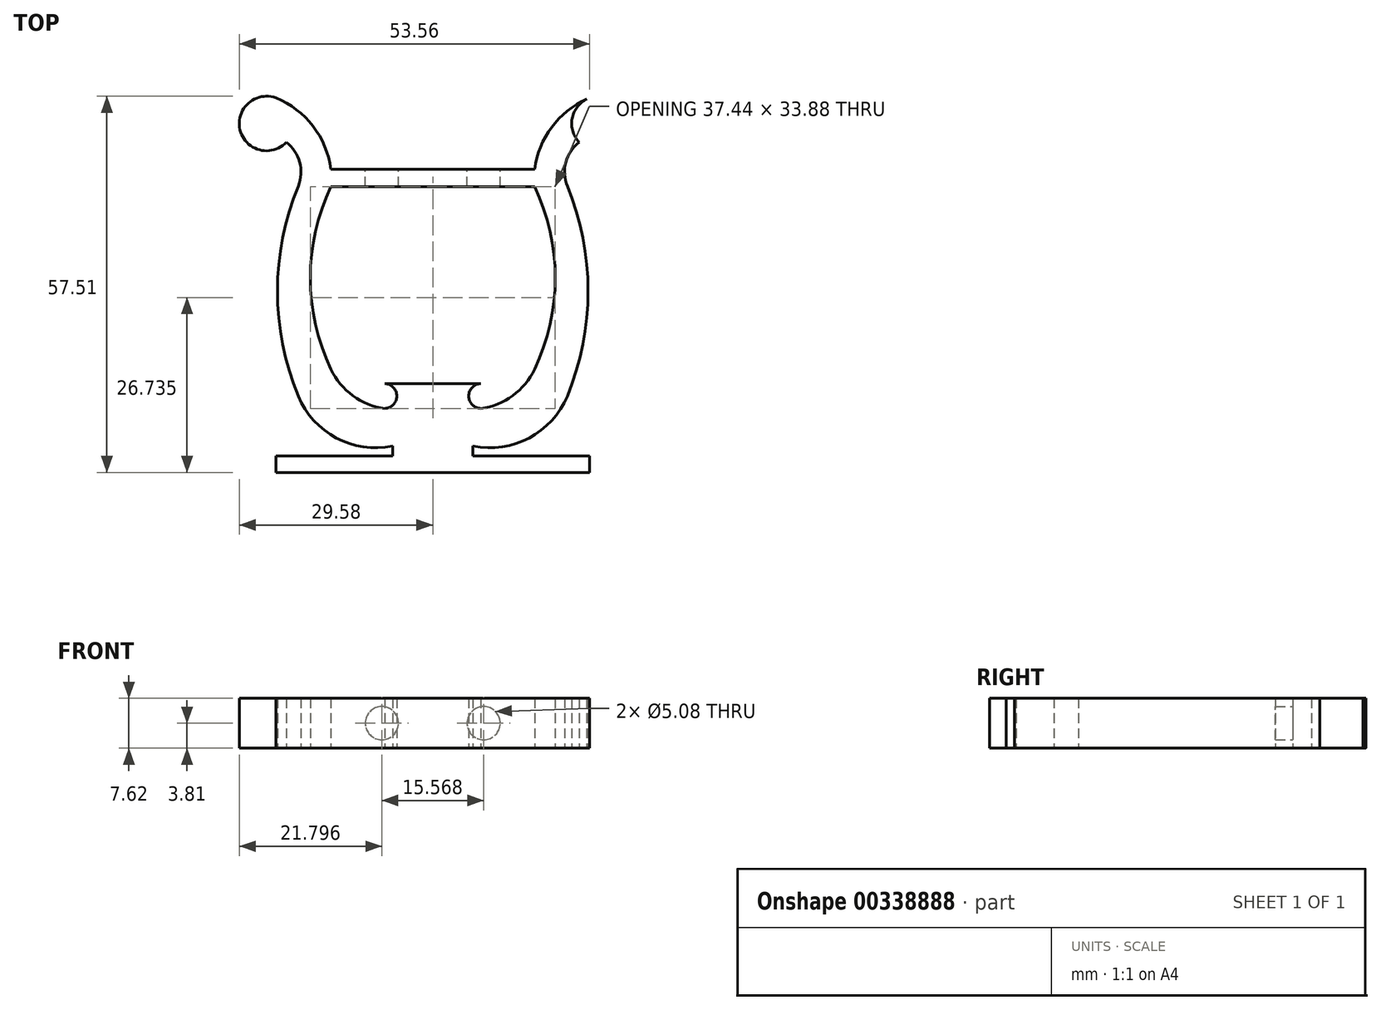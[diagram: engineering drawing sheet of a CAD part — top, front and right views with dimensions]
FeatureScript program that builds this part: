
annotation { "Feature Type Name" : "Feature", "Feature Type Description" : "" }
export const myFeature = defineFeature(function(context is Context, id is Id, definition is map)
    precondition{}
    {
        {
            var Q0;
            Q0=qCreatedBy(makeId("Top.planeOp"),FACE);
            var sketch = newSketch(context, id + "F0", { "sketchPlane" : qUnion([Q0])});
            skLineSegment(sketch, "E0", {"start": v(0, 25.38) * mm, "end": v(0, -25.42) * mm});
            skCircle(sketch, "E1", {"center": v(-25.4, 25.38) * mm, "radius": 4.17 * mm});
            skArc(sketch, "E2", {"start": v(-15.57, 18.4) * mm, "mid": v(-18.31, 24.98) * mm, "end": v(-23.98, 29.3) * mm});
            skArc(sketch, "E3", {"start": v(-20.58, 15.8) * mm, "mid": v(-20.35, 19.46) * mm, "end": v(-22.37, 22.51) * mm});
            skLineSegment(sketch, "E4", {"start": v(0, 18.4) * mm, "end": v(-15.57, 18.4) * mm});
            skLineSegment(sketch, "E5", {"start": v(0, 15.72) * mm, "end": v(-15.57, 15.72) * mm});
            skArc(sketch, "E6", {"start": v(-15.57, 15.72) * mm, "mid": v(-18.72, 1.77) * mm, "end": v(-15.57, -12.17) * mm});
            skArc(sketch, "E7", {"start": v(-20.58, 15.8) * mm, "mid": v(-23.74, -0.24) * mm, "end": v(-20.58, -16.28) * mm});
            skArc(sketch, "E8", {"start": v(-15.57, -12.17) * mm, "mid": v(-12.22, -16.21) * mm, "end": v(-7.35, -18.17) * mm});
            skArc(sketch, "E9", {"start": v(-7.35, -18.17) * mm, "mid": v(-5.5, -16.27) * mm, "end": v(-7.35, -14.37) * mm});
            skLineSegment(sketch, "E10", {"start": v(-7.35, -14.37) * mm, "end": v(0, -14.37) * mm});
            skArc(sketch, "E11", {"start": v(-20.58, -16.28) * mm, "mid": v(-14.74, -22.69) * mm, "end": v(-6.15, -23.9) * mm});
            skLineSegment(sketch, "E12", {"start": v(-6.15, -23.9) * mm, "end": v(-6.15, -25.42) * mm});
            skLineSegment(sketch, "E13", {"start": v(-6.15, -25.42) * mm, "end": v(-23.98, -25.42) * mm});
            skLineSegment(sketch, "E14", {"start": v(-23.98, -25.42) * mm, "end": v(-23.98, -27.96) * mm});
            skLineSegment(sketch, "E15", {"start": v(-23.98, -27.96) * mm, "end": v(0, -27.96) * mm});
            skArc(sketch, "E16.MirrorCS", {"start": v(15.57, 15.72) * mm, "mid": v(18.72, 1.77) * mm, "end": v(15.57, -12.17) * mm});
            skArc(sketch, "E17.MirrorCS", {"start": v(15.57, -12.17) * mm, "mid": v(12.22, -16.21) * mm, "end": v(7.35, -18.17) * mm});
            skLineSegment(sketch, "E18.MirrorCS", {"start": v(7.35, -14.37) * mm, "end": v(0, -14.37) * mm});
            skArc(sketch, "E19.MirrorCS", {"start": v(7.35, -18.17) * mm, "mid": v(5.5, -16.27) * mm, "end": v(7.35, -14.37) * mm});
            skArc(sketch, "E20.MirrorCS", {"start": v(20.58, -16.28) * mm, "mid": v(14.74, -22.69) * mm, "end": v(6.15, -23.9) * mm});
            skLineSegment(sketch, "E21.MirrorCS", {"start": v(6.15, -25.42) * mm, "end": v(23.98, -25.42) * mm});
            skLineSegment(sketch, "E22.MirrorCS", {"start": v(23.98, -27.96) * mm, "end": v(0, -27.96) * mm});
            skArc(sketch, "E23.MirrorCS", {"start": v(20.58, 15.8) * mm, "mid": v(23.74, -0.24) * mm, "end": v(20.58, -16.28) * mm});
            skLineSegment(sketch, "E24.MirrorCS", {"start": v(0, 15.72) * mm, "end": v(15.57, 15.72) * mm});
            skLineSegment(sketch, "E25.MirrorCS", {"start": v(0, 18.4) * mm, "end": v(15.57, 18.4) * mm});
            skArc(sketch, "E26.MirrorCS", {"start": v(15.57, 18.4) * mm, "mid": v(18.31, 24.98) * mm, "end": v(23.98, 29.3) * mm});
            skCircle(sketch, "E27.MirrorC", {"center": v(25.4, 25.38) * mm, "radius": 4.17 * mm});
            skLineSegment(sketch, "E28.MirrorCS", {"start": v(6.15, -23.9) * mm, "end": v(6.15, -25.42) * mm});
            skLineSegment(sketch, "E29.MirrorCS", {"start": v(23.98, -25.42) * mm, "end": v(23.98, -27.96) * mm});
            skArc(sketch, "E30.MirrorCS", {"start": v(20.58, 15.8) * mm, "mid": v(20.35, 19.46) * mm, "end": v(22.37, 22.51) * mm});
            skSolve(sketch);
        }
        {
            var Q0;
            {var subQ1=sQuery(id+"F0.wireOp",EDGE,"E3");Q0=makeQuery(id+"F0.imprint","IMPRINT",FACE,{"disambiguationData":[TD([[makeQuery(id+"F0.imprint","IMPRINT",EDGE,{"derivedFrom":subQ1}),-1.0]])]});}
            var Q1;
            {var subQ0=sQuery(id+"F0.wireOp",EDGE,"E27.MirrorC");var subQ1=sQuery(id+"F0.wireOp",EDGE,"E26.MirrorCS");var subQ2=makeQuery(id+"F0.imprint","INTERSECT",VERTEX,{"disambiguationData":[OD(0.0)],"derivedFrom":[subQ1,subQ0]});Q1=makeQuery(id+"F0.imprint","IMPRINT",FACE,{"disambiguationData":[TD([[makeQuery(id+"F0.imprint","IMPRINT",EDGE,{"disambiguationData":[TD([[subQ2,1.0]])],"derivedFrom":subQ1}),-1.0]])]});}
            var Q2;
            {var subQ0=sQuery(id+"F0.wireOp",EDGE,"E2");var subQ1=sQuery(id+"F0.wireOp",EDGE,"E1");var subQ2=makeQuery(id+"F0.imprint","INTERSECT",VERTEX,{"disambiguationData":[OD(0.0)],"derivedFrom":[subQ1,subQ0]});Q2=makeQuery(id+"F0.imprint","IMPRINT",FACE,{"disambiguationData":[TD([[makeQuery(id+"F0.imprint","IMPRINT",EDGE,{"disambiguationData":[TD([[subQ2,-1.0]])],"derivedFrom":subQ1}),1.0]])]});}
            extrude(context, id + "F1", {"entities" : qUnion([Q0, Q1, Q2]), "depth" : 7.62 * mm});
        }
        {
            var Q0;
            Q0=makeQuery(id+"F1.opExtrude","SWEPT_FACE",FACE,{"disambiguationData":[OSD([sQuery(id+"F0.wireOp",EDGE,"E4"),sQuery(id+"F0.wireOp",EDGE,"E25.MirrorCS")])]});
            var sketch = newSketch(context, id + "F2", { "sketchPlane" : qUnion([Q0])});
            skPoint(sketch, "E31", {"position": v(0, 0) * mm});
            skPoint(sketch, "E32", {"position": v(0, 7.62) * mm});
            skLineSegment(sketch, "E33", {"start": v(15.57, 3.81) * mm, "end": v(-15.57, 3.81) * mm});
            skPoint(sketch, "E34", {"position": v(0, 3.81) * mm});
            skLineSegment(sketch, "E35", {"start": v(15.57, 3.81) * mm, "end": v(0, 3.81) * mm});
            skLineSegment(sketch, "E36", {"start": v(0, 3.81) * mm, "end": v(-15.57, 3.81) * mm});
            skPoint(sketch, "E37", {"position": v(7.78, 3.81) * mm});
            skPoint(sketch, "E38", {"position": v(-7.78, 3.81) * mm});
            skSolve(sketch);
        }
        {
            var Q0;
            Q0=sQuery(id+"F2.wireOp",VERTEX,"E37");
            var Q1;
            Q1=makeQuery(id+"F1.opExtrude","SWEPT_BODY",BODY,{"disambiguationData":[OSD([sQuery(id+"F0.wireOp",EDGE,"E1"),sQuery(id+"F0.wireOp",EDGE,"E2"),sQuery(id+"F0.wireOp",EDGE,"E3"),sQuery(id+"F0.wireOp",EDGE,"E4"),sQuery(id+"F0.wireOp",EDGE,"E5"),sQuery(id+"F0.wireOp",EDGE,"E6"),sQuery(id+"F0.wireOp",EDGE,"E7"),sQuery(id+"F0.wireOp",EDGE,"E8"),sQuery(id+"F0.wireOp",EDGE,"E9"),sQuery(id+"F0.wireOp",EDGE,"E10"),sQuery(id+"F0.wireOp",EDGE,"E11"),sQuery(id+"F0.wireOp",EDGE,"E12"),sQuery(id+"F0.wireOp",EDGE,"E13"),sQuery(id+"F0.wireOp",EDGE,"E14"),sQuery(id+"F0.wireOp",EDGE,"E15"),sQuery(id+"F0.wireOp",EDGE,"E16.MirrorCS"),sQuery(id+"F0.wireOp",EDGE,"E17.MirrorCS"),sQuery(id+"F0.wireOp",EDGE,"E18.MirrorCS"),sQuery(id+"F0.wireOp",EDGE,"E19.MirrorCS"),sQuery(id+"F0.wireOp",EDGE,"E20.MirrorCS"),sQuery(id+"F0.wireOp",EDGE,"E21.MirrorCS"),sQuery(id+"F0.wireOp",EDGE,"E22.MirrorCS"),sQuery(id+"F0.wireOp",EDGE,"E23.MirrorCS"),sQuery(id+"F0.wireOp",EDGE,"E24.MirrorCS"),sQuery(id+"F0.wireOp",EDGE,"E25.MirrorCS"),sQuery(id+"F0.wireOp",EDGE,"E26.MirrorCS"),sQuery(id+"F0.wireOp",EDGE,"E27.MirrorC"),sQuery(id+"F0.wireOp",EDGE,"E28.MirrorCS"),sQuery(id+"F0.wireOp",EDGE,"E29.MirrorCS"),sQuery(id+"F0.wireOp",EDGE,"E30.MirrorCS")])]});
            hole(context, id + "F3", {"style" : HoleStyle.SIMPLE, "endStyle" : HoleEndStyle.BLIND, "holeDiameter" : 5.08 * mm, "holeDepth" : 12.7 * mm, "isTappedThrough" : true, "tappedDepth" : 12.7 * mm, "tapClearance" : 3, "locations" : qUnion([Q0]), "scope" : qUnion([Q1])});
        }
        {
            var Q0;
            Q0=sQuery(id+"F2.wireOp",VERTEX,"E38");
            var Q1;
            Q1=makeQuery(id+"F1.opExtrude","SWEPT_BODY",BODY,{"disambiguationData":[OSD([sQuery(id+"F0.wireOp",EDGE,"E1"),sQuery(id+"F0.wireOp",EDGE,"E2"),sQuery(id+"F0.wireOp",EDGE,"E3"),sQuery(id+"F0.wireOp",EDGE,"E4"),sQuery(id+"F0.wireOp",EDGE,"E5"),sQuery(id+"F0.wireOp",EDGE,"E6"),sQuery(id+"F0.wireOp",EDGE,"E7"),sQuery(id+"F0.wireOp",EDGE,"E8"),sQuery(id+"F0.wireOp",EDGE,"E9"),sQuery(id+"F0.wireOp",EDGE,"E10"),sQuery(id+"F0.wireOp",EDGE,"E11"),sQuery(id+"F0.wireOp",EDGE,"E12"),sQuery(id+"F0.wireOp",EDGE,"E13"),sQuery(id+"F0.wireOp",EDGE,"E14"),sQuery(id+"F0.wireOp",EDGE,"E15"),sQuery(id+"F0.wireOp",EDGE,"E16.MirrorCS"),sQuery(id+"F0.wireOp",EDGE,"E17.MirrorCS"),sQuery(id+"F0.wireOp",EDGE,"E18.MirrorCS"),sQuery(id+"F0.wireOp",EDGE,"E19.MirrorCS"),sQuery(id+"F0.wireOp",EDGE,"E20.MirrorCS"),sQuery(id+"F0.wireOp",EDGE,"E21.MirrorCS"),sQuery(id+"F0.wireOp",EDGE,"E22.MirrorCS"),sQuery(id+"F0.wireOp",EDGE,"E23.MirrorCS"),sQuery(id+"F0.wireOp",EDGE,"E24.MirrorCS"),sQuery(id+"F0.wireOp",EDGE,"E25.MirrorCS"),sQuery(id+"F0.wireOp",EDGE,"E26.MirrorCS"),sQuery(id+"F0.wireOp",EDGE,"E27.MirrorC"),sQuery(id+"F0.wireOp",EDGE,"E28.MirrorCS"),sQuery(id+"F0.wireOp",EDGE,"E29.MirrorCS"),sQuery(id+"F0.wireOp",EDGE,"E30.MirrorCS")])]});
            hole(context, id + "F4", {"style" : HoleStyle.SIMPLE, "endStyle" : HoleEndStyle.BLIND, "holeDiameter" : 5.08 * mm, "holeDepth" : 12.7 * mm, "isTappedThrough" : true, "tappedDepth" : 12.7 * mm, "tapClearance" : 3, "locations" : qUnion([Q0]), "scope" : qUnion([Q1])});
        }
    });
